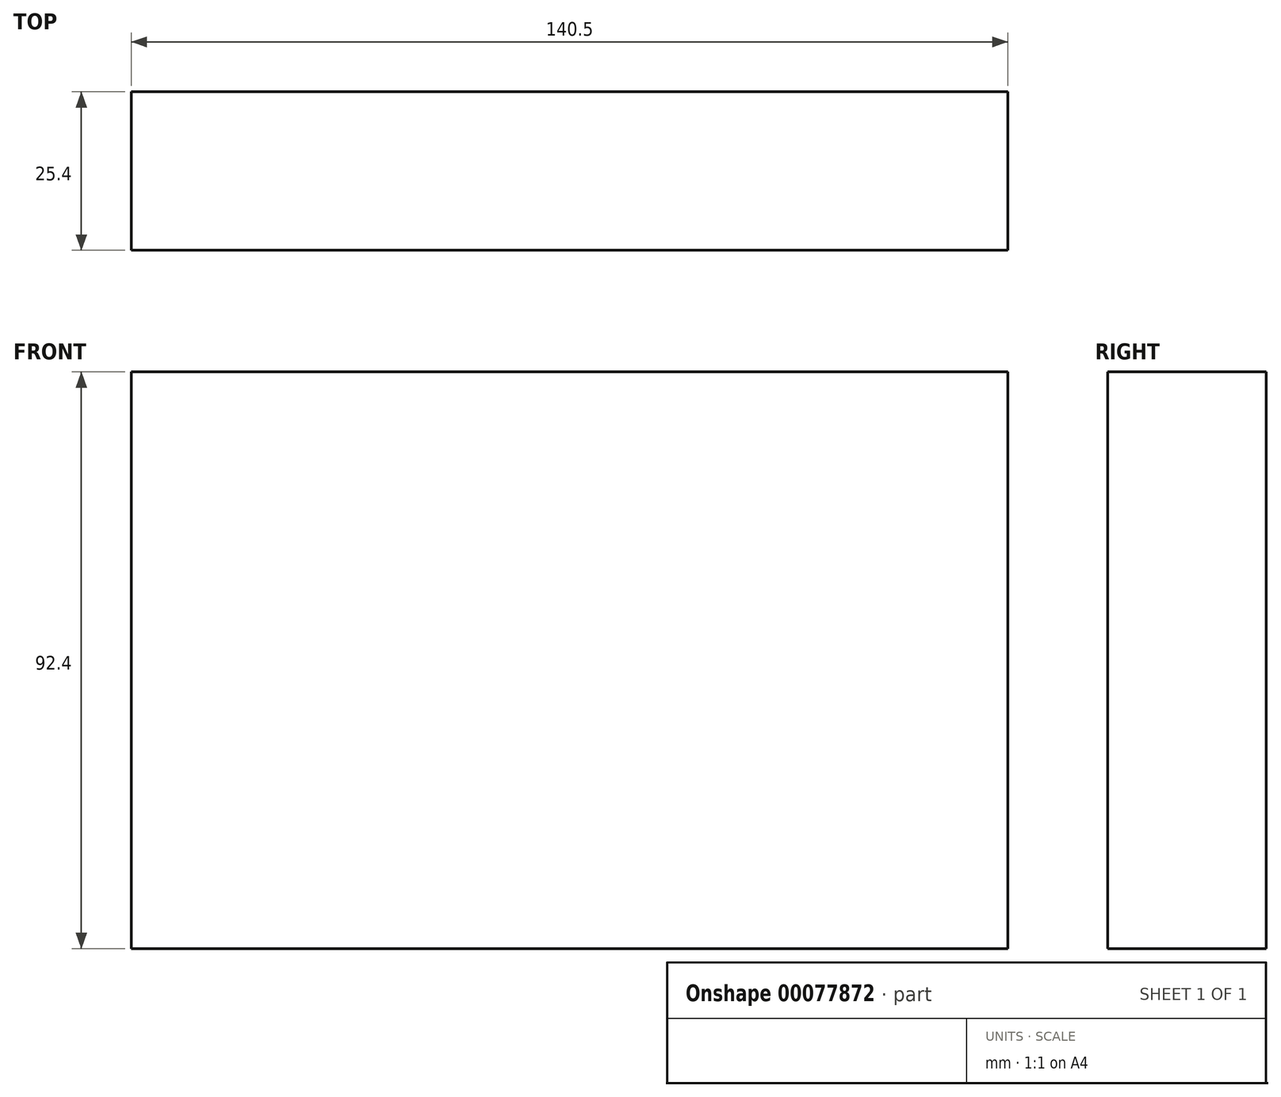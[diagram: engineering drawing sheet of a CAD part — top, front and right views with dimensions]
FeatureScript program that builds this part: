
annotation { "Feature Type Name" : "Feature", "Feature Type Description" : "" }
export const myFeature = defineFeature(function(context is Context, id is Id, definition is map)
    precondition{}
    {
        {
            var Q0;
            Q0=qCreatedBy(makeId("Front.planeOp"),FACE);
            var sketch = newSketch(context, id + "F0", { "sketchPlane" : qUnion([Q0])});
            skLineSegment(sketch, "E0.bottom", {"start": v(-58.93, 70.4) * mm, "end": v(81.57, 70.4) * mm});
            skLineSegment(sketch, "E0.top", {"start": v(-58.93, -22) * mm, "end": v(81.57, -22) * mm});
            skLineSegment(sketch, "E0.left", {"start": v(-58.93, 70.4) * mm, "end": v(-58.93, -22) * mm});
            skLineSegment(sketch, "E0.right", {"start": v(81.57, 70.4) * mm, "end": v(81.57, -22) * mm});
            skSolve(sketch);
        }
        {
            var Q0;
            Q0=makeQuery(id+"F0.imprint","IMPRINT",FACE,{"disambiguationData":[TD([[makeQuery(id+"F0.imprint","IMPRINT",EDGE,{"derivedFrom":sQuery(id+"F0.wireOp",EDGE,"E0.bottom")}),-1.0]])]});
            extrude(context, id + "F1", {"entities" : qUnion([Q0]), "depth" : 25.4 * mm});
        }
        {
            var Q0;
            Q0=makeQuery(id+"F1.opExtrude","SWEPT_FACE",FACE,{"disambiguationData":[OSD([sQuery(id+"F0.wireOp",EDGE,"E0.bottom")])]});
            var sketch = newSketch(context, id + "F2", { "sketchPlane" : qUnion([Q0])});
            skCircle(sketch, "E1", {"center": v(-7.7, -12.96) * mm, "radius": 4.32 * mm});
            skSolve(sketch);
        }
        {
            var Q0;
            Q0=sQuery(id+"F2.wireOp",EDGE,"E1");
            extrude(context, id + "F3", {"bodyType" : ToolBodyType.SURFACE, "surfaceEntities" : qUnion([Q0]), "depth" : 25.4 * mm});
        }
    });
